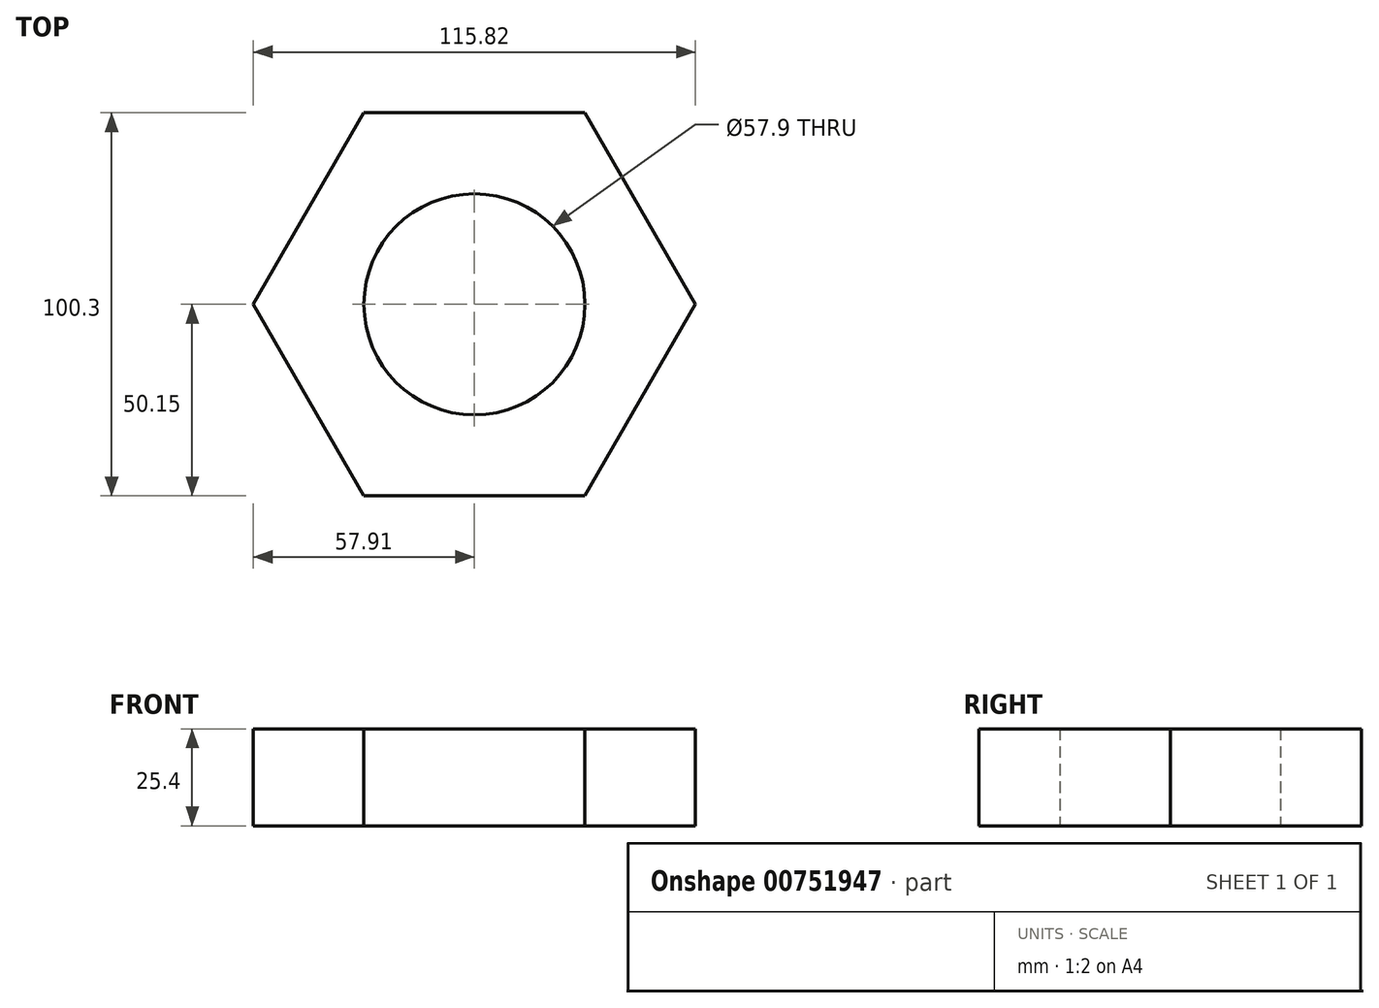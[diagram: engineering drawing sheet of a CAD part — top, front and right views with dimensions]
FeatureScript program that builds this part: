
annotation { "Feature Type Name" : "Feature", "Feature Type Description" : "" }
export const myFeature = defineFeature(function(context is Context, id is Id, definition is map)
    precondition{}
    {
        {
            var Q0;
            Q0=qCreatedBy(makeId("Top.planeOp"),FACE);
            var sketch = newSketch(context, id + "F0", { "sketchPlane" : qUnion([Q0])});
            skCircle(sketch, "E0.cCircle", {"center": v(0, 0) * mm, "radius": 50.15 * mm, "construction": true});
            skLineSegment(sketch, "E0.0", {"start": v(-28.96, 50.15) * mm, "end": v(28.96, 50.15) * mm});
            skLineSegment(sketch, "E0.1", {"start": v(28.96, 50.15) * mm, "end": v(57.91, 0) * mm});
            skLineSegment(sketch, "E0.2", {"start": v(57.91, 0) * mm, "end": v(28.96, -50.15) * mm});
            skLineSegment(sketch, "E0.3", {"start": v(28.96, -50.15) * mm, "end": v(-28.96, -50.15) * mm});
            skLineSegment(sketch, "E0.4", {"start": v(-28.96, -50.15) * mm, "end": v(-57.91, 0) * mm});
            skLineSegment(sketch, "E0.5", {"start": v(-57.91, 0) * mm, "end": v(-28.96, 50.15) * mm});
            skPoint(sketch, "E0.0.midPoint", {"position": v(0, 50.15) * mm});
            skCircle(sketch, "E1", {"center": v(0, 0) * mm, "radius": 28.95 * mm});
            skSolve(sketch);
        }
        {
            var Q0;
            Q0=makeQuery(id+"F0.imprint","IMPRINT",FACE,{"disambiguationData":[TD([[makeQuery(id+"F0.imprint","IMPRINT",EDGE,{"derivedFrom":sQuery(id+"F0.wireOp",EDGE,"E0.0")}),-1.0]])]});
            extrude(context, id + "F1", {"entities" : qUnion([Q0]), "depth" : 25.4 * mm, "offsetDistance" : 25.4 * mm});
        }
    });
